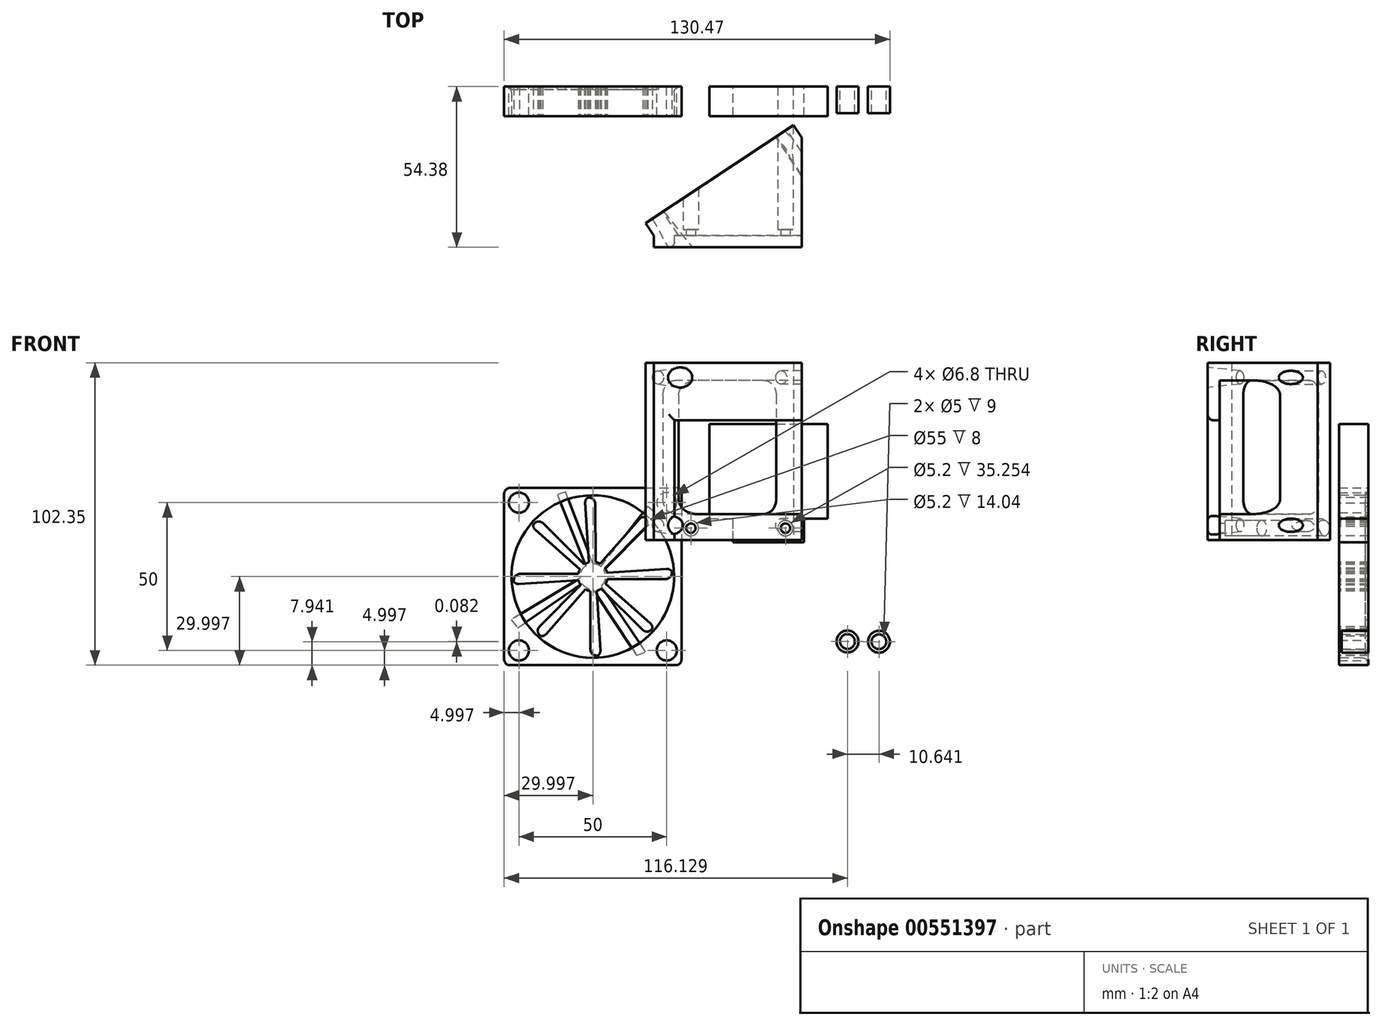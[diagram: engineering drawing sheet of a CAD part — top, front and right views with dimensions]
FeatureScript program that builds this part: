
annotation { "Feature Type Name" : "Feature", "Feature Type Description" : "" }
export const myFeature = defineFeature(function(context is Context, id is Id, definition is map)
    precondition{}
    {
        {
            var Q0;
            Q0=qCreatedBy(makeId("Front.planeOp"),FACE);
            var sketch = newSketch(context, id + "F0", { "sketchPlane" : qUnion([Q0])});
            skLineSegment(sketch, "E0.bottom", {"start": v(-24.18, 39.22) * mm, "end": v(15.82, 39.22) * mm});
            skLineSegment(sketch, "E0.top", {"start": v(-24.18, -0.78) * mm, "end": v(15.82, -0.78) * mm});
            skLineSegment(sketch, "E0.left", {"start": v(-24.18, 39.22) * mm, "end": v(-24.18, -0.78) * mm});
            skLineSegment(sketch, "E0.right", {"start": v(15.82, 39.22) * mm, "end": v(15.82, -0.78) * mm});
            skLineSegment(sketch, "E1.bottom", {"start": v(15.82, -0.78) * mm, "end": v(7.82, -0.78) * mm});
            skLineSegment(sketch, "E1.top", {"start": v(15.82, 7.22) * mm, "end": v(7.82, 7.22) * mm});
            skLineSegment(sketch, "E1.left", {"start": v(15.82, -0.78) * mm, "end": v(15.82, 7.22) * mm});
            skLineSegment(sketch, "E1.right", {"start": v(7.82, -0.78) * mm, "end": v(7.82, 7.22) * mm});
            skLineSegment(sketch, "E2.bottom", {"start": v(-24.18, -0.78) * mm, "end": v(-16.18, -0.78) * mm});
            skLineSegment(sketch, "E2.top", {"start": v(-24.18, 7.22) * mm, "end": v(-16.18, 7.22) * mm});
            skLineSegment(sketch, "E2.left", {"start": v(-24.18, -0.78) * mm, "end": v(-24.18, 7.22) * mm});
            skLineSegment(sketch, "E2.right", {"start": v(-16.18, -0.78) * mm, "end": v(-16.18, 7.22) * mm});
            skCircle(sketch, "E3", {"center": v(-20.18, 3.22) * mm, "radius": 2.5 * mm});
            skPoint(sketch, "E3.centerSnap0", {"position": v(-16.18, 3.22) * mm});
            skPoint(sketch, "E3.centerSnap1", {"position": v(-20.18, 7.22) * mm});
            skCircle(sketch, "E4", {"center": v(11.82, 3.22) * mm, "radius": 2.5 * mm});
            skPoint(sketch, "E4.centerSnap0", {"position": v(7.82, 3.22) * mm});
            skPoint(sketch, "E4.centerSnap1", {"position": v(11.82, 7.22) * mm});
            skSolve(sketch);
        }
        {
            var Q0;
            Q0=makeQuery(id+"F0.imprint","IMPRINT",FACE,{"disambiguationData":[TD([[makeQuery(id+"F0.imprint","IMPRINT",EDGE,{"derivedFrom":sQuery(id+"F0.wireOp",EDGE,"E1.bottom")}),-1.0]])]});
            var Q1;
            Q1=makeQuery(id+"F0.imprint","IMPRINT",FACE,{"disambiguationData":[TD([[makeQuery(id+"F0.imprint","IMPRINT",EDGE,{"derivedFrom":sQuery(id+"F0.wireOp",EDGE,"E2.bottom")}),1.0]])]});
            var Q2;
            Q2=makeQuery(id+"F0.imprint","IMPRINT",FACE,{"disambiguationData":[TD([[makeQuery(id+"F0.imprint","IMPRINT",EDGE,{"derivedFrom":sQuery(id+"F0.wireOp",EDGE,"E0.bottom")}),-1.0]])]});
            extrude(context, id + "F1", {"entities" : qUnion([Q0, Q1, Q2]), "depth" : 1 * mm, "offsetDistance" : 25 * mm});
        }
        {
            var Q0;
            Q0=makeQuery(id+"F0.imprint","IMPRINT",FACE,{"disambiguationData":[TD([[makeQuery(id+"F0.imprint","IMPRINT",EDGE,{"derivedFrom":sQuery(id+"F0.wireOp",EDGE,"E0.bottom")}),-1.0]])]});
            extrude(context, id + "F2", {"entities" : qUnion([Q0]), "operationType" : NewBodyOperationType.ADD, "depth" : 10 * mm, "offsetDistance" : 25 * mm});
        }
        {
            var Q0;
            Q0=qCreatedBy(makeId("Front.planeOp"),FACE);
            var sketch = newSketch(context, id + "F3", { "sketchPlane" : qUnion([Q0])});
            skLineSegment(sketch, "E5.bottom", {"start": v(-93.6, 17.65) * mm, "end": v(-33.6, 17.65) * mm});
            skLineSegment(sketch, "E5.top", {"start": v(-93.6, -42.35) * mm, "end": v(-33.6, -42.35) * mm});
            skLineSegment(sketch, "E5.left", {"start": v(-93.6, 17.65) * mm, "end": v(-93.6, -42.35) * mm});
            skLineSegment(sketch, "E5.right", {"start": v(-33.6, 17.65) * mm, "end": v(-33.6, -42.35) * mm});
            skCircle(sketch, "E6", {"center": v(-88.6, -37.35) * mm, "radius": 3.4 * mm});
            skCircle(sketch, "E7", {"center": v(-88.6, 12.65) * mm, "radius": 3.4 * mm});
            skCircle(sketch, "E8", {"center": v(-38.6, 12.65) * mm, "radius": 3.4 * mm});
            skCircle(sketch, "E9", {"center": v(-38.6, -37.35) * mm, "radius": 3.4 * mm});
            skSolve(sketch);
        }
        {
            var Q0;
            Q0=makeQuery(id+"F3.imprint","IMPRINT",FACE,{"disambiguationData":[TD([[makeQuery(id+"F3.imprint","IMPRINT",EDGE,{"derivedFrom":sQuery(id+"F3.wireOp",EDGE,"E5.bottom")}),-1.0]])]});
            extrude(context, id + "F4", {"entities" : qUnion([Q0]), "operationType" : NewBodyOperationType.ADD, "depth" : 10 * mm, "offsetDistance" : 25 * mm});
        }
        {
            var Q0;
            Q0=qCreatedBy(makeId("Front.planeOp"),FACE);
            var sketch = newSketch(context, id + "F5", { "sketchPlane" : qUnion([Q0])});
            skCircle(sketch, "E10", {"center": v(22.54, -34.33) * mm, "radius": 2.5 * mm});
            skCircle(sketch, "E11.0", {"center": v(22.54, -34.33) * mm, "radius": 3.7 * mm});
            skCircle(sketch, "E12", {"center": v(33.18, -34.4) * mm, "radius": 2.5 * mm});
            skCircle(sketch, "E13.0", {"center": v(33.18, -34.4) * mm, "radius": 3.7 * mm});
            skSolve(sketch);
        }
        {
            var Q0;
            Q0=makeQuery(id+"F5.imprint","IMPRINT",FACE,{"disambiguationData":[TD([[makeQuery(id+"F5.imprint","IMPRINT",EDGE,{"derivedFrom":sQuery(id+"F5.wireOp",EDGE,"E10")}),-1.0]])]});
            var Q1;
            Q1=makeQuery(id+"F5.imprint","IMPRINT",FACE,{"disambiguationData":[TD([[makeQuery(id+"F5.imprint","IMPRINT",EDGE,{"derivedFrom":sQuery(id+"F5.wireOp",EDGE,"E12")}),-1.0]])]});
            extrude(context, id + "F6", {"entities" : qUnion([Q0, Q1]), "depth" : 9 * mm, "offsetDistance" : 25 * mm});
        }
        {
            var Q0;
            Q0=qCreatedBy(makeId("Top.planeOp"),FACE);
            var sketch = newSketch(context, id + "F7", { "sketchPlane" : qUnion([Q0])});
            skLineSegment(sketch, "E14", {"start": v(-42.94, -50.38) * mm, "end": v(7.06, -50.38) * mm});
            skLineSegment(sketch, "E15", {"start": v(7.06, -50.38) * mm, "end": v(7.06, -17.22) * mm});
            skLineSegment(sketch, "E16", {"start": v(7.06, -17.22) * mm, "end": v(-42.94, -50.38) * mm});
            skSolve(sketch);
        }
        {
            var Q0;
            Q0=makeQuery(id+"F7.imprint","IMPRINT",FACE,{"disambiguationData":[TD([[makeQuery(id+"F7.imprint","IMPRINT",EDGE,{"derivedFrom":sQuery(id+"F7.wireOp",EDGE,"E14")}),1.0]])]});
            extrude(context, id + "F8", {"entities" : qUnion([Q0]), "depth" : 60 * mm, "offsetDistance" : 25 * mm});
        }
        {
            var Q0;
            Q0=makeQuery(id+"F8.opExtrude","SWEPT_FACE",FACE,{"disambiguationData":[OSD([sQuery(id+"F7.wireOp",EDGE,"E16")])]});
            extrude(context, id + "F9", {"entities" : qUnion([Q0]), "operationType" : NewBodyOperationType.ADD, "depth" : 5 * mm, "offsetDistance" : 25 * mm});
        }
        {
            var Q0;
            Q0=makeQuery(id+"F9.opExtrude","CAP_FACE",FACE,{"disambiguationData":[OSD([sQuery(id+"F7.wireOp",EDGE,"E16")])],"isStart":false});
            var sketch = newSketch(context, id + "F10", { "sketchPlane" : qUnion([Q0])});
            skCircle(sketch, "E17", {"center": v(58.64, 55) * mm, "radius": 2.25 * mm});
            skCircle(sketch, "E18", {"center": v(8.64, 55) * mm, "radius": 2.25 * mm});
            skCircle(sketch, "E19", {"center": v(8.64, 5) * mm, "radius": 2.25 * mm});
            skCircle(sketch, "E20", {"center": v(58.64, 5) * mm, "radius": 2.25 * mm});
            skLineSegment(sketch, "E21.bottom", {"start": v(15.64, 54) * mm, "end": v(51.64, 54) * mm});
            skLineSegment(sketch, "E21.top", {"start": v(15.64, 8.8) * mm, "end": v(51.64, 8.8) * mm});
            skLineSegment(sketch, "E21.left", {"start": v(10.64, 49) * mm, "end": v(10.64, 13.8) * mm});
            skLineSegment(sketch, "E21.right", {"start": v(56.64, 49) * mm, "end": v(56.64, 13.8) * mm});
            skPoint(sketch, "E22.visualSharp", {"position": v(10.64, 54) * mm});
            skArc(sketch, "E22.filletArc", {"start": v(15.64, 54) * mm, "mid": v(12.1, 52.54) * mm, "end": v(10.64, 49) * mm});
            skPoint(sketch, "E23.visualSharp", {"position": v(10.64, 8.8) * mm});
            skArc(sketch, "E23.filletArc", {"start": v(10.64, 13.8) * mm, "mid": v(12.1, 10.26) * mm, "end": v(15.64, 8.8) * mm});
            skPoint(sketch, "E24.visualSharp", {"position": v(56.64, 8.8) * mm});
            skArc(sketch, "E24.filletArc", {"start": v(51.64, 8.8) * mm, "mid": v(55.17, 10.26) * mm, "end": v(56.64, 13.8) * mm});
            skPoint(sketch, "E25.visualSharp", {"position": v(56.64, 54) * mm});
            skArc(sketch, "E25.filletArc", {"start": v(56.64, 49) * mm, "mid": v(55.17, 52.54) * mm, "end": v(51.64, 54) * mm});
            skSolve(sketch);
        }
        {
            var Q0;
            Q0=makeQuery(id+"F8.opExtrude","SWEPT_FACE",FACE,{"disambiguationData":[OSD([sQuery(id+"F7.wireOp",EDGE,"E14")])]});
            var sketch = newSketch(context, id + "F11", { "sketchPlane" : qUnion([Q0])});
            skCircle(sketch, "E26", {"center": v(-30.44, 4) * mm, "radius": 2.6 * mm});
            skCircle(sketch, "E27", {"center": v(1.56, 4) * mm, "radius": 2.6 * mm});
            skCircle(sketch, "E28.0", {"center": v(-30.44, 4) * mm, "radius": 1.6 * mm});
            skCircle(sketch, "E29.0", {"center": v(1.56, 4) * mm, "radius": 1.6 * mm});
            skLineSegment(sketch, "E30.bottom", {"start": v(7.06, 0) * mm, "end": v(-35.94, 0) * mm});
            skLineSegment(sketch, "E30.top", {"start": v(7.06, 40.5) * mm, "end": v(-35.94, 40.5) * mm});
            skLineSegment(sketch, "E30.left", {"start": v(7.06, 0) * mm, "end": v(7.06, 40.5) * mm});
            skLineSegment(sketch, "E30.right", {"start": v(-35.94, 0) * mm, "end": v(-35.94, 40.5) * mm});
            skSolve(sketch);
        }
        {
            var Q0;
            Q0=makeQuery(id+"F10.imprint","IMPRINT",FACE,{"disambiguationData":[TD([[makeQuery(id+"F10.imprint","IMPRINT",EDGE,{"derivedFrom":sQuery(id+"F10.wireOp",EDGE,"E19")}),1.0]])]});
            var Q1;
            Q1=makeQuery(id+"F10.imprint","IMPRINT",FACE,{"disambiguationData":[TD([[makeQuery(id+"F10.imprint","IMPRINT",EDGE,{"derivedFrom":sQuery(id+"F10.wireOp",EDGE,"E18")}),1.0]])]});
            var Q2;
            Q2=makeQuery(id+"F10.imprint","IMPRINT",FACE,{"disambiguationData":[TD([[makeQuery(id+"F10.imprint","IMPRINT",EDGE,{"derivedFrom":sQuery(id+"F10.wireOp",EDGE,"E17")}),1.0]])]});
            var Q3;
            Q3=makeQuery(id+"F10.imprint","IMPRINT",FACE,{"disambiguationData":[TD([[makeQuery(id+"F10.imprint","IMPRINT",EDGE,{"derivedFrom":sQuery(id+"F10.wireOp",EDGE,"E20")}),1.0]])]});
            var Q4;
            Q4=makeQuery(id+"F10.imprint","IMPRINT",FACE,{"disambiguationData":[TD([[makeQuery(id+"F10.imprint","IMPRINT",EDGE,{"derivedFrom":sQuery(id+"F10.wireOp",EDGE,"E21.bottom")}),-1.0]])]});
            extrude(context, id + "F12", {"entities" : qUnion([Q0, Q1, Q2, Q3, Q4]), "operationType" : NewBodyOperationType.REMOVE, "oppositeDirection" : true, "depth" : 50 * mm, "offsetDistance" : 25 * mm});
        }
        {
            var Q0;
            Q0=makeQuery(id+"F11.imprint","IMPRINT",FACE,{"disambiguationData":[TD([[makeQuery(id+"F11.imprint","IMPRINT",EDGE,{"derivedFrom":sQuery(id+"F11.wireOp",EDGE,"E26")}),1.0]])]});
            var Q1;
            Q1=makeQuery(id+"F11.imprint","IMPRINT",FACE,{"disambiguationData":[TD([[makeQuery(id+"F11.imprint","IMPRINT",EDGE,{"derivedFrom":sQuery(id+"F11.wireOp",EDGE,"E28.0")}),1.0]])]});
            var Q2;
            Q2=makeQuery(id+"F11.imprint","IMPRINT",FACE,{"disambiguationData":[TD([[makeQuery(id+"F11.imprint","IMPRINT",EDGE,{"derivedFrom":sQuery(id+"F11.wireOp",EDGE,"E29.0")}),1.0]])]});
            var Q3;
            Q3=makeQuery(id+"F11.imprint","IMPRINT",FACE,{"disambiguationData":[TD([[makeQuery(id+"F11.imprint","IMPRINT",EDGE,{"derivedFrom":sQuery(id+"F11.wireOp",EDGE,"E27")}),1.0]])]});
            extrude(context, id + "F13", {"entities" : qUnion([Q0, Q1, Q2, Q3]), "operationType" : NewBodyOperationType.REMOVE, "oppositeDirection" : true, "depth" : 53.98 * mm, "offsetDistance" : 25 * mm});
        }
        {
            var Q0;
            Q0=makeQuery(id+"F11.imprint","IMPRINT",FACE,{"disambiguationData":[TD([[makeQuery(id+"F11.imprint","IMPRINT",EDGE,{"derivedFrom":sQuery(id+"F11.wireOp",EDGE,"E27")}),1.0]])]});
            var Q1;
            Q1=makeQuery(id+"F11.imprint","IMPRINT",FACE,{"disambiguationData":[TD([[makeQuery(id+"F11.imprint","IMPRINT",EDGE,{"derivedFrom":sQuery(id+"F11.wireOp",EDGE,"E26")}),1.0]])]});
            extrude(context, id + "F14", {"entities" : qUnion([Q0, Q1]), "operationType" : NewBodyOperationType.ADD, "oppositeDirection" : true, "depth" : 2 * mm, "offsetDistance" : 25 * mm});
        }
        {
            var Q0;
            {var subQ7=sQuery(id+"F11.wireOp",EDGE,"E30.top");Q0=makeQuery(id+"F11.imprint","IMPRINT",FACE,{"disambiguationData":[TD([[makeQuery(id+"F11.imprint","IMPRINT",EDGE,{"derivedFrom":subQ7}),-1.0]])]});}
            extrude(context, id + "F15", {"entities" : qUnion([Q0]), "operationType" : NewBodyOperationType.ADD, "depth" : 4 * mm, "offsetDistance" : 25 * mm});
        }
        {
            var Q0;
            Q0=makeQuery(id+"F15.opExtrude","CAP_EDGE",EDGE,{"disambiguationData":[OSD([sQuery(id+"F11.wireOp",EDGE,"E30.top")])],"isStart":false});
            var Q1;
            Q1=makeQuery(id+"F15.opExtrude","CAP_EDGE",EDGE,{"disambiguationData":[OSD([sQuery(id+"F11.wireOp",EDGE,"E30.right")])],"isStart":false});
            fillet(context, id + "F16", {"entities" : qUnion([Q0, Q1]), "radius" : 2 * mm, "tangentPropagation" : true, "allowEdgeOverflow" : false});
        }
        {
            var Q0;
            Q0=makeQuery(id+"F10.imprint","IMPRINT",FACE,{"disambiguationData":[TD([[makeQuery(id+"F10.imprint","IMPRINT",EDGE,{"derivedFrom":sQuery(id+"F10.wireOp",EDGE,"E20")}),1.0]])]});
            var Q1;
            Q1=makeQuery(id+"F10.imprint","IMPRINT",FACE,{"disambiguationData":[TD([[makeQuery(id+"F10.imprint","IMPRINT",EDGE,{"derivedFrom":sQuery(id+"F10.wireOp",EDGE,"E17")}),1.0]])]});
            extrude(context, id + "F17", {"entities" : qUnion([Q0, Q1]), "operationType" : NewBodyOperationType.REMOVE, "oppositeDirection" : true, "depth" : 30.96 * mm, "offsetDistance" : 25 * mm, "hasDraft" : true, "draftAngle" : 5 * degree});
        }
        {
            var Q0;
            Q0=makeQuery(id+"F4.opExtrude","SWEPT_EDGE",EDGE,{"disambiguationData":[OSD([sQuery(id+"F3.wireOp",EDGE,"E5.bottom"),sQuery(id+"F3.wireOp",EDGE,"E5.left")])]});
            var Q1;
            Q1=makeQuery(id+"F4.opExtrude","SWEPT_EDGE",EDGE,{"disambiguationData":[OSD([sQuery(id+"F3.wireOp",EDGE,"E5.bottom"),sQuery(id+"F3.wireOp",EDGE,"E5.right")])]});
            var Q2;
            Q2=makeQuery(id+"F4.opExtrude","SWEPT_EDGE",EDGE,{"disambiguationData":[OSD([sQuery(id+"F3.wireOp",EDGE,"E5.top"),sQuery(id+"F3.wireOp",EDGE,"E5.right")])]});
            var Q3;
            Q3=makeQuery(id+"F4.opExtrude","SWEPT_EDGE",EDGE,{"disambiguationData":[OSD([sQuery(id+"F3.wireOp",EDGE,"E5.top"),sQuery(id+"F3.wireOp",EDGE,"E5.left")])]});
            fillet(context, id + "F18", {"entities" : qUnion([Q0, Q1, Q2, Q3]), "radius" : 2 * mm, "tangentPropagation" : true, "allowEdgeOverflow" : false});
        }
        {
            var Q0;
            Q0=makeQuery(id+"F4.opExtrude","CAP_FACE",FACE,{"disambiguationData":[OSD([sQuery(id+"F3.wireOp",EDGE,"E5.bottom"),sQuery(id+"F3.wireOp",EDGE,"E5.top"),sQuery(id+"F3.wireOp",EDGE,"E5.left"),sQuery(id+"F3.wireOp",EDGE,"E5.right"),sQuery(id+"F3.wireOp",EDGE,"E6"),sQuery(id+"F3.wireOp",EDGE,"E7"),sQuery(id+"F3.wireOp",EDGE,"E8"),sQuery(id+"F3.wireOp",EDGE,"E9")])],"isStart":false});
            var sketch = newSketch(context, id + "F19", { "sketchPlane" : qUnion([Q0])});
            skCircle(sketch, "E31", {"center": v(-63.6, -12.35) * mm, "radius": 27.5 * mm});
            skCircle(sketch, "E32", {"center": v(-63.6, -12.35) * mm, "radius": 5 * mm});
            skSolve(sketch);
        }
        {
            var Q0;
            Q0=makeQuery(id+"F19.imprint","IMPRINT",FACE,{"disambiguationData":[TD([[makeQuery(id+"F19.imprint","IMPRINT",EDGE,{"derivedFrom":sQuery(id+"F19.wireOp",EDGE,"E31")}),1.0]])]});
            extrude(context, id + "F20", {"entities" : qUnion([Q0]), "operationType" : NewBodyOperationType.REMOVE, "oppositeDirection" : true, "depth" : 25 * mm, "offsetDistance" : 25 * mm});
        }
        {
            var Q0;
            Q0=makeQuery(id+"F20.boolean.opBoolean","COPY",EDGE,{"derivedFrom":makeQuery(id+"F20.opExtrude","CAP_EDGE",EDGE,{"disambiguationData":[OSD([sQuery(id+"F19.wireOp",EDGE,"E31")])],"isStart":true})});
            var Q1;
            Q1=makeQuery(id+"F20.boolean.opBoolean","INTERSECT",EDGE,{"derivedFrom":[makeQuery(id+"F4.opExtrude","CAP_FACE",FACE,{"disambiguationData":[OSD([sQuery(id+"F3.wireOp",EDGE,"E5.bottom"),sQuery(id+"F3.wireOp",EDGE,"E5.top"),sQuery(id+"F3.wireOp",EDGE,"E5.left"),sQuery(id+"F3.wireOp",EDGE,"E5.right"),sQuery(id+"F3.wireOp",EDGE,"E6"),sQuery(id+"F3.wireOp",EDGE,"E7"),sQuery(id+"F3.wireOp",EDGE,"E8"),sQuery(id+"F3.wireOp",EDGE,"E9")])],"isStart":true}),makeQuery(id+"F20.opExtrude","SWEPT_FACE",FACE,{"disambiguationData":[OSD([sQuery(id+"F19.wireOp",EDGE,"E31")])]})]});
            fillet(context, id + "F21", {"entities" : qUnion([Q0, Q1]), "radius" : 2 * mm, "tangentPropagation" : true, "allowEdgeOverflow" : false});
        }
        {
            var Q0;
            Q0=makeQuery(id+"F20.boolean.opBoolean","SPLIT",FACE,{"disambiguationData":[TD([makeQuery(id+"F20.opExtrude","SWEPT_FACE",FACE,{"disambiguationData":[OSD([sQuery(id+"F19.wireOp",EDGE,"E32")])]})])],"derivedFrom":makeQuery(id+"F4.opExtrude","CAP_FACE",FACE,{"disambiguationData":[OSD([sQuery(id+"F3.wireOp",EDGE,"E5.bottom"),sQuery(id+"F3.wireOp",EDGE,"E5.top"),sQuery(id+"F3.wireOp",EDGE,"E5.left"),sQuery(id+"F3.wireOp",EDGE,"E5.right"),sQuery(id+"F3.wireOp",EDGE,"E6"),sQuery(id+"F3.wireOp",EDGE,"E7"),sQuery(id+"F3.wireOp",EDGE,"E8"),sQuery(id+"F3.wireOp",EDGE,"E9")])],"isStart":false})});
            var sketch = newSketch(context, id + "F22", { "sketchPlane" : qUnion([Q0])});
            skArc(sketch, "E33", {"start": v(-62.7, -7.43) * mm, "mid": v(-63.8, -7.4) * mm, "end": v(-64.89, -7.52) * mm});
            skLineSegment(sketch, "E34", {"start": v(-64.89, -7.52) * mm, "end": v(-66.15, 12.64) * mm});
            skLineSegment(sketch, "E35", {"start": v(-65.47, 14.27) * mm, "end": v(-65.4, 14.33) * mm});
            skLineSegment(sketch, "E36", {"start": v(-65.4, 14.33) * mm, "end": v(-64.88, 14.36) * mm});
            skLineSegment(sketch, "E37", {"start": v(-62.85, 12.89) * mm, "end": v(-62.74, 12.47) * mm});
            skLineSegment(sketch, "E38", {"start": v(-62.74, 12.47) * mm, "end": v(-62.7, -7.43) * mm});
            skPoint(sketch, "E39.visualSharp", {"position": v(-66.2, 13.62) * mm});
            skArc(sketch, "E39.filletArc", {"start": v(-65.47, 14.27) * mm, "mid": v(-66, 13.53) * mm, "end": v(-66.15, 12.64) * mm});
            skPoint(sketch, "E40.visualSharp", {"position": v(-63.27, 14.44) * mm});
            skArc(sketch, "E40.filletArc", {"start": v(-62.85, 12.89) * mm, "mid": v(-63.6, 13.98) * mm, "end": v(-64.88, 14.36) * mm});
            skSolve(sketch);
        }
        {
            var Q0;
            {var subQ0=sQuery(id+"F22.wireOp",EDGE,"E34");Q0=makeQuery(id+"F22.imprint","IMPRINT",FACE,{"disambiguationData":[TD([[makeQuery(id+"F22.imprint","IMPRINT",EDGE,{"derivedFrom":subQ0}),-1.0]])]});}
            extrude(context, id + "F23", {"entities" : qUnion([Q0]), "oppositeDirection" : true, "depth" : 10 * mm, "offsetDistance" : 25 * mm});
        }
        {
            var Q0;
            Q0=makeQuery(id+"F23.opExtrude","SWEPT_BODY",BODY,{"disambiguationData":[OSD([sQuery(id+"F19.wireOp",EDGE,"E32"),sQuery(id+"F22.wireOp",EDGE,"E34"),sQuery(id+"F22.wireOp",EDGE,"E35"),sQuery(id+"F22.wireOp",EDGE,"E36"),sQuery(id+"F22.wireOp",EDGE,"E37"),sQuery(id+"F22.wireOp",EDGE,"E38"),sQuery(id+"F22.wireOp",EDGE,"E39.filletArc"),sQuery(id+"F22.wireOp",EDGE,"E40.filletArc")])]});
            var Q1;
            Q1=makeQuery(id+"F20.boolean.opBoolean","COPY",EDGE,{"derivedFrom":makeQuery(id+"F20.opExtrude","CAP_EDGE",EDGE,{"disambiguationData":[OSD([sQuery(id+"F19.wireOp",EDGE,"E32")])],"isStart":true})});
            circularPattern(context, id + "F24", {"operationType" : NewBodyOperationType.ADD, "entities" : qUnion([Q0]), "axis" : qUnion([Q1]), "angle" : 360 * degree, "instanceCount" : 8, "equalSpace" : true});
        }
        {
            var Q0;
            Q0=makeQuery(id+"F24.opPattern","COPY",BODY,{"derivedFrom":makeQuery(id+"F23.opExtrude","SWEPT_BODY",BODY,{"disambiguationData":[OSD([sQuery(id+"F19.wireOp",EDGE,"E32"),sQuery(id+"F22.wireOp",EDGE,"E34"),sQuery(id+"F22.wireOp",EDGE,"E35"),sQuery(id+"F22.wireOp",EDGE,"E36"),sQuery(id+"F22.wireOp",EDGE,"E37"),sQuery(id+"F22.wireOp",EDGE,"E38"),sQuery(id+"F22.wireOp",EDGE,"E39.filletArc"),sQuery(id+"F22.wireOp",EDGE,"E40.filletArc")])]}),"instanceName":"3"});
            var Q1;
            Q1=makeQuery(id+"F24.opPattern","COPY",BODY,{"derivedFrom":makeQuery(id+"F23.opExtrude","SWEPT_BODY",BODY,{"disambiguationData":[OSD([sQuery(id+"F19.wireOp",EDGE,"E32"),sQuery(id+"F22.wireOp",EDGE,"E34"),sQuery(id+"F22.wireOp",EDGE,"E35"),sQuery(id+"F22.wireOp",EDGE,"E36"),sQuery(id+"F22.wireOp",EDGE,"E37"),sQuery(id+"F22.wireOp",EDGE,"E38"),sQuery(id+"F22.wireOp",EDGE,"E39.filletArc"),sQuery(id+"F22.wireOp",EDGE,"E40.filletArc")])]}),"instanceName":"2"});
            var Q2;
            Q2=makeQuery(id+"F24.opPattern","COPY",BODY,{"derivedFrom":makeQuery(id+"F23.opExtrude","SWEPT_BODY",BODY,{"disambiguationData":[OSD([sQuery(id+"F19.wireOp",EDGE,"E32"),sQuery(id+"F22.wireOp",EDGE,"E34"),sQuery(id+"F22.wireOp",EDGE,"E35"),sQuery(id+"F22.wireOp",EDGE,"E36"),sQuery(id+"F22.wireOp",EDGE,"E37"),sQuery(id+"F22.wireOp",EDGE,"E38"),sQuery(id+"F22.wireOp",EDGE,"E39.filletArc"),sQuery(id+"F22.wireOp",EDGE,"E40.filletArc")])]}),"instanceName":"1"});
            var Q3;
            Q3=makeQuery(id+"F23.opExtrude","SWEPT_BODY",BODY,{"disambiguationData":[OSD([sQuery(id+"F19.wireOp",EDGE,"E32"),sQuery(id+"F22.wireOp",EDGE,"E34"),sQuery(id+"F22.wireOp",EDGE,"E35"),sQuery(id+"F22.wireOp",EDGE,"E36"),sQuery(id+"F22.wireOp",EDGE,"E37"),sQuery(id+"F22.wireOp",EDGE,"E38"),sQuery(id+"F22.wireOp",EDGE,"E39.filletArc"),sQuery(id+"F22.wireOp",EDGE,"E40.filletArc")])]});
            var Q4;
            Q4=makeQuery(id+"F24.opPattern","COPY",BODY,{"derivedFrom":makeQuery(id+"F23.opExtrude","SWEPT_BODY",BODY,{"disambiguationData":[OSD([sQuery(id+"F19.wireOp",EDGE,"E32"),sQuery(id+"F22.wireOp",EDGE,"E34"),sQuery(id+"F22.wireOp",EDGE,"E35"),sQuery(id+"F22.wireOp",EDGE,"E36"),sQuery(id+"F22.wireOp",EDGE,"E37"),sQuery(id+"F22.wireOp",EDGE,"E38"),sQuery(id+"F22.wireOp",EDGE,"E39.filletArc"),sQuery(id+"F22.wireOp",EDGE,"E40.filletArc")])]}),"instanceName":"7"});
            var Q5;
            Q5=makeQuery(id+"F24.opPattern","COPY",BODY,{"derivedFrom":makeQuery(id+"F23.opExtrude","SWEPT_BODY",BODY,{"disambiguationData":[OSD([sQuery(id+"F19.wireOp",EDGE,"E32"),sQuery(id+"F22.wireOp",EDGE,"E34"),sQuery(id+"F22.wireOp",EDGE,"E35"),sQuery(id+"F22.wireOp",EDGE,"E36"),sQuery(id+"F22.wireOp",EDGE,"E37"),sQuery(id+"F22.wireOp",EDGE,"E38"),sQuery(id+"F22.wireOp",EDGE,"E39.filletArc"),sQuery(id+"F22.wireOp",EDGE,"E40.filletArc")])]}),"instanceName":"6"});
            var Q6;
            Q6=makeQuery(id+"F24.opPattern","COPY",BODY,{"derivedFrom":makeQuery(id+"F23.opExtrude","SWEPT_BODY",BODY,{"disambiguationData":[OSD([sQuery(id+"F19.wireOp",EDGE,"E32"),sQuery(id+"F22.wireOp",EDGE,"E34"),sQuery(id+"F22.wireOp",EDGE,"E35"),sQuery(id+"F22.wireOp",EDGE,"E36"),sQuery(id+"F22.wireOp",EDGE,"E37"),sQuery(id+"F22.wireOp",EDGE,"E38"),sQuery(id+"F22.wireOp",EDGE,"E39.filletArc"),sQuery(id+"F22.wireOp",EDGE,"E40.filletArc")])]}),"instanceName":"5"});
            var Q7;
            Q7=makeQuery(id+"F24.opPattern","COPY",BODY,{"derivedFrom":makeQuery(id+"F23.opExtrude","SWEPT_BODY",BODY,{"disambiguationData":[OSD([sQuery(id+"F19.wireOp",EDGE,"E32"),sQuery(id+"F22.wireOp",EDGE,"E34"),sQuery(id+"F22.wireOp",EDGE,"E35"),sQuery(id+"F22.wireOp",EDGE,"E36"),sQuery(id+"F22.wireOp",EDGE,"E37"),sQuery(id+"F22.wireOp",EDGE,"E38"),sQuery(id+"F22.wireOp",EDGE,"E39.filletArc"),sQuery(id+"F22.wireOp",EDGE,"E40.filletArc")])]}),"instanceName":"4"});
            var Q8;
            Q8=makeQuery(id+"F20.boolean.opBoolean","SPLIT",BODY,{"disambiguationData":[OD(1.0)],"derivedFrom":makeQuery(id+"F4.opExtrude","SWEPT_BODY",BODY,{"disambiguationData":[OSD([sQuery(id+"F3.wireOp",EDGE,"E5.bottom"),sQuery(id+"F3.wireOp",EDGE,"E5.top"),sQuery(id+"F3.wireOp",EDGE,"E5.left"),sQuery(id+"F3.wireOp",EDGE,"E5.right"),sQuery(id+"F3.wireOp",EDGE,"E6"),sQuery(id+"F3.wireOp",EDGE,"E7"),sQuery(id+"F3.wireOp",EDGE,"E8"),sQuery(id+"F3.wireOp",EDGE,"E9")])]})});
            booleanBodies(context, id + "F25", {"operationType" : BooleanOperationType.UNION, "tools" : qUnion([Q0, Q1, Q2, Q3, Q4, Q5, Q6, Q7, Q8])});
        }
        {
            var Q0;
            {var subQ0=sQuery(id+"F19.wireOp",EDGE,"E32");var subQ1=makeQuery(id+"F23.opExtrude","CAP_FACE",FACE,{"disambiguationData":[OSD([subQ0,sQuery(id+"F22.wireOp",EDGE,"E34"),sQuery(id+"F22.wireOp",EDGE,"E35"),sQuery(id+"F22.wireOp",EDGE,"E36"),sQuery(id+"F22.wireOp",EDGE,"E37"),sQuery(id+"F22.wireOp",EDGE,"E38"),sQuery(id+"F22.wireOp",EDGE,"E39.filletArc"),sQuery(id+"F22.wireOp",EDGE,"E40.filletArc")])],"isStart":false});Q0=makeQuery(id+"F25.opBoolean","MERGE",FACE,{"derivedFrom":[makeQuery(id+"F20.boolean.opBoolean","SPLIT",FACE,{"disambiguationData":[TD([makeQuery(id+"F20.opExtrude","SWEPT_FACE",FACE,{"disambiguationData":[OSD([subQ0])]})])],"derivedFrom":makeQuery(id+"F4.opExtrude","CAP_FACE",FACE,{"disambiguationData":[OSD([sQuery(id+"F3.wireOp",EDGE,"E5.bottom"),sQuery(id+"F3.wireOp",EDGE,"E5.top"),sQuery(id+"F3.wireOp",EDGE,"E5.left"),sQuery(id+"F3.wireOp",EDGE,"E5.right"),sQuery(id+"F3.wireOp",EDGE,"E6"),sQuery(id+"F3.wireOp",EDGE,"E7"),sQuery(id+"F3.wireOp",EDGE,"E8"),sQuery(id+"F3.wireOp",EDGE,"E9")])],"isStart":true})}),subQ1,makeQuery(id+"F24.opPattern","COPY",FACE,{"derivedFrom":subQ1,"instanceName":"1"}),makeQuery(id+"F24.opPattern","COPY",FACE,{"derivedFrom":subQ1,"instanceName":"2"}),makeQuery(id+"F24.opPattern","COPY",FACE,{"derivedFrom":subQ1,"instanceName":"3"}),makeQuery(id+"F24.opPattern","COPY",FACE,{"derivedFrom":subQ1,"instanceName":"4"}),makeQuery(id+"F24.opPattern","COPY",FACE,{"derivedFrom":subQ1,"instanceName":"5"}),makeQuery(id+"F24.opPattern","COPY",FACE,{"derivedFrom":subQ1,"instanceName":"6"}),makeQuery(id+"F24.opPattern","COPY",FACE,{"derivedFrom":subQ1,"instanceName":"7"})]});}
            var sketch = newSketch(context, id + "F26", { "sketchPlane" : qUnion([Q0])});
            skArc(sketch, "E41", {"start": v(59.88, -10.15) * mm, "mid": v(59.33, -13.03) * mm, "end": v(60.75, -15.6) * mm});
            skLineSegment(sketch, "E42", {"start": v(63.6, -8.03) * mm, "end": v(72.86, 16.25) * mm});
            skLineSegment(sketch, "E43", {"start": v(72.86, 16.25) * mm, "end": v(75.65, 15.42) * mm});
            skLineSegment(sketch, "E44", {"start": v(75.65, 15.42) * mm, "end": v(65.95, -8.74) * mm});
            skLineSegment(sketch, "E45", {"start": v(63.65, -16.67) * mm, "end": v(48.76, -38.97) * mm});
            skLineSegment(sketch, "E46", {"start": v(48.76, -38.97) * mm, "end": v(45.72, -37.86) * mm});
            skLineSegment(sketch, "E47", {"start": v(45.72, -37.86) * mm, "end": v(60.75, -15.6) * mm});
            skLineSegment(sketch, "E48", {"start": v(67.89, -12.84) * mm, "end": v(91.17, -26.92) * mm});
            skLineSegment(sketch, "E49", {"start": v(91.17, -26.92) * mm, "end": v(89.03, -29.76) * mm});
            skLineSegment(sketch, "E50", {"start": v(89.03, -29.76) * mm, "end": v(67.24, -14.67) * mm});
            skLineSegment(sketch, "E51", {"start": v(60.9, -8.98) * mm, "end": v(45, 11.38) * mm});
            skLineSegment(sketch, "E52", {"start": v(45, 11.38) * mm, "end": v(41.37, 8.4) * mm});
            skLineSegment(sketch, "E53", {"start": v(41.37, 8.4) * mm, "end": v(59.88, -10.15) * mm});
            skArc(sketch, "E54.trimOffspring", {"start": v(63.6, -8.03) * mm, "mid": v(62.17, -8.28) * mm, "end": v(60.9, -8.98) * mm});
            skArc(sketch, "E55.trimOffspring", {"start": v(63.65, -16.67) * mm, "mid": v(65.7, -16.13) * mm, "end": v(67.24, -14.67) * mm});
            skArc(sketch, "E56.trimOffspring", {"start": v(67.89, -12.84) * mm, "mid": v(67.5, -10.51) * mm, "end": v(65.95, -8.74) * mm});
            skSolve(sketch);
        }
        {
            var Q0;
            {var subQ50=sQuery(id+"F26.wireOp",EDGE,"E41");Q0=makeQuery(id+"F26.imprint","IMPRINT",FACE,{"disambiguationData":[TD([[makeQuery(id+"F26.imprint","IMPRINT",EDGE,{"derivedFrom":subQ50}),1.0]])]});}
            var Q1;
            {var subQ19=sQuery(id+"F26.wireOp",EDGE,"E52");Q1=makeQuery(id+"F26.imprint","IMPRINT",FACE,{"disambiguationData":[TD([[makeQuery(id+"F26.imprint","IMPRINT",EDGE,{"derivedFrom":subQ19}),1.0]])]});}
            var Q2;
            {var subQ1=sQuery(id+"F26.wireOp",EDGE,"E46");Q2=makeQuery(id+"F26.imprint","IMPRINT",FACE,{"disambiguationData":[TD([[makeQuery(id+"F26.imprint","IMPRINT",EDGE,{"derivedFrom":subQ1}),-1.0]])]});}
            var Q3;
            {var subQ1=sQuery(id+"F26.wireOp",EDGE,"E49");Q3=makeQuery(id+"F26.imprint","IMPRINT",FACE,{"disambiguationData":[TD([[makeQuery(id+"F26.imprint","IMPRINT",EDGE,{"derivedFrom":subQ1}),-1.0]])]});}
            var Q4;
            {var subQ12=sQuery(id+"F26.wireOp",EDGE,"E43");Q4=makeQuery(id+"F26.imprint","IMPRINT",FACE,{"disambiguationData":[TD([[makeQuery(id+"F26.imprint","IMPRINT",EDGE,{"derivedFrom":subQ12}),-1.0]])]});}
            extrude(context, id + "F27", {"entities" : qUnion([Q0, Q1, Q2, Q3, Q4]), "oppositeDirection" : true, "depth" : 1 * mm, "offsetDistance" : 25 * mm});
        }
    });
